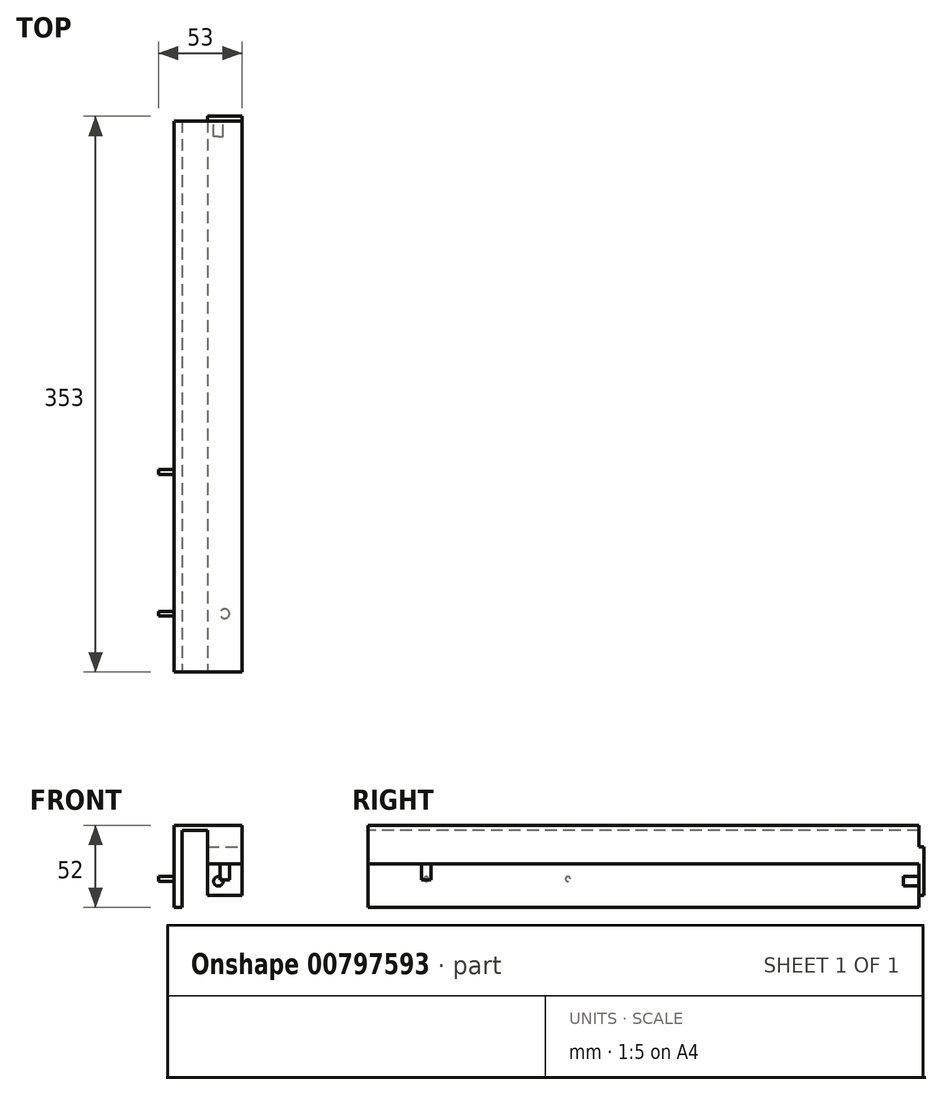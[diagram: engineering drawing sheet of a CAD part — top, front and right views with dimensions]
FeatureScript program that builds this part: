
annotation { "Feature Type Name" : "Feature", "Feature Type Description" : "" }
export const myFeature = defineFeature(function(context is Context, id is Id, definition is map)
    precondition{}
    {
        {
            var Q0;
            Q0=qCreatedBy(makeId("Top.planeOp"),FACE);
            var sketch = newSketch(context, id + "F0", { "sketchPlane" : qUnion([Q0])});
            skLineSegment(sketch, "E0.bottom", {"start": v(-3, 175) * mm, "end": v(0, 175) * mm});
            skLineSegment(sketch, "E0.top", {"start": v(-3, -175) * mm, "end": v(0, -175) * mm});
            skLineSegment(sketch, "E0.left", {"start": v(-3, 175) * mm, "end": v(-3, -175) * mm});
            skLineSegment(sketch, "E0.right", {"start": v(0, 175) * mm, "end": v(0, -175) * mm});
            skSolve(sketch);
        }
        {
            var Q0;
            Q0=makeQuery(id+"F0.imprint","IMPRINT",FACE,{"disambiguationData":[TD([[makeQuery(id+"F0.imprint","IMPRINT",EDGE,{"derivedFrom":sQuery(id+"F0.wireOp",EDGE,"E0.bottom")}),-1.0]])]});
            extrude(context, id + "F1", {"entities" : qUnion([Q0]), "depth" : 52 * mm, "offsetDistance" : 25 * mm});
        }
        {
            var Q0;
            Q0=makeQuery(id+"F1.opExtrude","SWEPT_FACE",FACE,{"disambiguationData":[OSD([sQuery(id+"F0.wireOp",EDGE,"E0.right")])]});
            var sketch = newSketch(context, id + "F2", { "sketchPlane" : qUnion([Q0])});
            skLineSegment(sketch, "E1", {"start": v(175, 49) * mm, "end": v(-175, 49) * mm});
            skSolve(sketch);
        }
        {
            var Q0;
            {var subQ0=sQuery(id+"F2.wireOp",EDGE,"E1");Q0=makeQuery(id+"F2.imprint","IMPRINT",FACE,{"disambiguationData":[TD([[makeQuery(id+"F2.imprint","IMPRINT",EDGE,{"derivedFrom":subQ0}),-1.0]])]});}
            extrude(context, id + "F3", {"entities" : qUnion([Q0]), "operationType" : NewBodyOperationType.ADD, "depth" : 40 * mm, "offsetDistance" : 25 * mm});
        }
        {
            var Q0;
            Q0=makeQuery(id+"F3.opExtrude","SWEPT_FACE",FACE,{"disambiguationData":[OSD([sQuery(id+"F2.wireOp",EDGE,"E1")])]});
            var sketch = newSketch(context, id + "F4", { "sketchPlane" : qUnion([Q0])});
            skLineSegment(sketch, "E2", {"start": v(18, -175) * mm, "end": v(18, 175) * mm});
            skSolve(sketch);
        }
        {
            var Q0;
            {var subQ0=sQuery(id+"F4.wireOp",EDGE,"E2");Q0=makeQuery(id+"F4.imprint","IMPRINT",FACE,{"disambiguationData":[TD([[makeQuery(id+"F4.imprint","IMPRINT",EDGE,{"derivedFrom":subQ0}),-1.0]])]});}
            extrude(context, id + "F5", {"entities" : qUnion([Q0]), "operationType" : NewBodyOperationType.ADD, "depth" : 21.5 * mm, "offsetDistance" : 25 * mm});
        }
        {
            var Q0;
            Q0=makeQuery(id+"F1.opExtrude","SWEPT_FACE",FACE,{"disambiguationData":[OSD([sQuery(id+"F0.wireOp",EDGE,"E0.left")])]});
            var sketch = newSketch(context, id + "F6", { "sketchPlane" : qUnion([Q0])});
            skLineSegment(sketch, "E3", {"start": v(175, 18) * mm, "end": v(-175, 18) * mm, "construction": true});
            skLineSegment(sketch, "E4", {"start": v(138, 18) * mm, "end": v(138, 0) * mm, "construction": true});
            skLineSegment(sketch, "E5", {"start": v(48, 18) * mm, "end": v(48, 0) * mm, "construction": true});
            skCircle(sketch, "E6", {"center": v(48, 18) * mm, "radius": 1.5 * mm});
            skCircle(sketch, "E7", {"center": v(138, 18) * mm, "radius": 1.5 * mm});
            skSolve(sketch);
        }
        {
            var Q0;
            Q0=makeQuery(id+"F6.imprint","IMPRINT",FACE,{"disambiguationData":[TD([[makeQuery(id+"F6.imprint","IMPRINT",EDGE,{"derivedFrom":sQuery(id+"F6.wireOp",EDGE,"E7")}),1.0]])]});
            var Q1;
            Q1=makeQuery(id+"F6.imprint","IMPRINT",FACE,{"disambiguationData":[TD([[makeQuery(id+"F6.imprint","IMPRINT",EDGE,{"derivedFrom":sQuery(id+"F6.wireOp",EDGE,"E6")}),1.0]])]});
            extrude(context, id + "F7", {"entities" : qUnion([Q0, Q1]), "operationType" : NewBodyOperationType.ADD, "depth" : 10 * mm, "offsetDistance" : 25 * mm});
        }
        {
            var Q0;
            {var subQ0=sQuery(id+"F0.wireOp",EDGE,"E0.right");var subQ1=sQuery(id+"F0.wireOp",EDGE,"E0.bottom");Q0=makeQuery(id+"F5.boolean.opBoolean","MERGE",FACE,{"derivedFrom":[makeQuery(id+"F3.boolean.opBoolean","MERGE",FACE,{"derivedFrom":[makeQuery(id+"F1.opExtrude","SWEPT_FACE",FACE,{"disambiguationData":[OSD([subQ1])]}),makeQuery(id+"F3.opExtrude","SWEPT_FACE",FACE,{"disambiguationData":[OSD([subQ1,subQ0])]})]}),makeQuery(id+"F5.opExtrude","SWEPT_FACE",FACE,{"disambiguationData":[OSD([subQ1,subQ0,sQuery(id+"F2.wireOp",EDGE,"E1")])]})]});}
            var sketch = newSketch(context, id + "F8", { "sketchPlane" : qUnion([Q0])});
            skLineSegment(sketch, "E8", {"start": v(-18, 38.25) * mm, "end": v(-40, 38.25) * mm});
            skSolve(sketch);
        }
        {
            var Q0;
            Q0 = qSketchRegion(id + "F8", true);
            var Q1;
            {var subQ0=sQuery(id+"F8.wireOp",EDGE,"E8");Q1=makeQuery(id+"F8.imprint","IMPRINT",FACE,{"disambiguationData":[TD([[makeQuery(id+"F8.imprint","IMPRINT",EDGE,{"derivedFrom":subQ0}),1.0]])]});}
            extrude(context, id + "F9", {"entities" : qUnion([Q0, Q1]), "depth" : 3 * mm, "offsetDistance" : 25 * mm});
        }
        {
            var Q0;
            {var subQ0=sQuery(id+"F2.wireOp",EDGE,"E1");var subQ1=sQuery(id+"F0.wireOp",EDGE,"E0.right");var subQ2=sQuery(id+"F0.wireOp",EDGE,"E0.bottom");Q0=makeQuery(id+"F9.opExtrude","SWEPT_FACE",FACE,{"disambiguationData":[OSD([subQ2,subQ1,subQ0]),TDD([makeQuery(id+"F8.imprint","IMPRINT",EDGE,{"derivedFrom":makeQuery(id+"F5.opExtrude","CAP_EDGE",EDGE,{"disambiguationData":[OSD([subQ2,subQ1,subQ0])],"isStart":false})})])]});}
            extrude(context, id + "F10", {"entities" : qUnion([Q0]), "operationType" : NewBodyOperationType.ADD, "depth" : 20 * mm, "offsetDistance" : 25 * mm});
        }
        {
            var Q0;
            {var subQ0=sQuery(id+"F2.wireOp",EDGE,"E1");var subQ1=sQuery(id+"F0.wireOp",EDGE,"E0.right");var subQ2=sQuery(id+"F0.wireOp",EDGE,"E0.bottom");Q0=makeQuery(id+"F10.boolean.opBoolean","MERGE",FACE,{"derivedFrom":[makeQuery(id+"F9.opExtrude","CAP_FACE",FACE,{"disambiguationData":[OSD([subQ2,subQ1,subQ0,sQuery(id+"F4.wireOp",EDGE,"E2"),sQuery(id+"F8.wireOp",EDGE,"E8")])],"isStart":true}),makeQuery(id+"F10.opExtrude","SWEPT_FACE",FACE,{"disambiguationData":[OSD([subQ2,subQ1,subQ0]),TDD([makeQuery(id+"F9.opExtrude","CAP_EDGE",EDGE,{"disambiguationData":[OSD([subQ2,subQ1,subQ0]),TDD([makeQuery(id+"F8.imprint","IMPRINT",EDGE,{"derivedFrom":makeQuery(id+"F5.opExtrude","CAP_EDGE",EDGE,{"disambiguationData":[OSD([subQ2,subQ1,subQ0])],"isStart":false})})])],"isStart":true})])]})]});}
            var sketch = newSketch(context, id + "F11", { "sketchPlane" : qUnion([Q0])});
            skLineSegment(sketch, "E9.0", {"start": v(40, 27.5) * mm, "end": v(18, 27.5) * mm, "construction": true});
            skLineSegment(sketch, "E10", {"start": v(40, 16.5) * mm, "end": v(18, 16.5) * mm, "construction": true});
            skLineSegment(sketch, "E11", {"start": v(25, 7.5) * mm, "end": v(25, 27.5) * mm, "construction": true});
            skCircle(sketch, "E12", {"center": v(25, 16.5) * mm, "radius": 3 * mm});
            skSolve(sketch);
        }
        {
            var Q0;
            Q0=makeQuery(id+"F11.imprint","IMPRINT",FACE,{"disambiguationData":[TD([[makeQuery(id+"F11.imprint","IMPRINT",EDGE,{"derivedFrom":sQuery(id+"F11.wireOp",EDGE,"E12")}),1.0]])]});
            extrude(context, id + "F12", {"entities" : qUnion([Q0]), "operationType" : NewBodyOperationType.ADD, "depth" : 10 * mm, "offsetDistance" : 25 * mm});
        }
        {
            var Q0;
            Q0=makeQuery(id+"F5.opExtrude","CAP_FACE",FACE,{"disambiguationData":[OSD([sQuery(id+"F0.wireOp",EDGE,"E0.bottom"),sQuery(id+"F0.wireOp",EDGE,"E0.top"),sQuery(id+"F0.wireOp",EDGE,"E0.right"),sQuery(id+"F2.wireOp",EDGE,"E1"),sQuery(id+"F4.wireOp",EDGE,"E2")])],"isStart":false});
            var sketch = newSketch(context, id + "F13", { "sketchPlane" : qUnion([Q0])});
            skLineSegment(sketch, "E13", {"start": v(18, 138) * mm, "end": v(40, 138) * mm, "construction": true});
            skCircle(sketch, "E14", {"center": v(29, 138) * mm, "radius": 3 * mm});
            skSolve(sketch);
        }
        {
            var Q0;
            Q0=makeQuery(id+"F13.imprint","IMPRINT",FACE,{"disambiguationData":[TD([[makeQuery(id+"F13.imprint","IMPRINT",EDGE,{"derivedFrom":sQuery(id+"F13.wireOp",EDGE,"E14")}),1.0]])]});
            extrude(context, id + "F14", {"entities" : qUnion([Q0]), "operationType" : NewBodyOperationType.ADD, "depth" : 10 * mm, "offsetDistance" : 25 * mm});
        }
        {
            var Q0;
            Q0=makeQuery(id+"F1.opExtrude","SWEPT_FACE",FACE,{"disambiguationData":[OSD([sQuery(id+"F0.wireOp",EDGE,"E0.right")])]});
            extrude(context, id + "F15", {"entities" : qUnion([Q0]), "operationType" : NewBodyOperationType.ADD, "depth" : 2 * mm, "offsetDistance" : 25 * mm});
        }
    });
